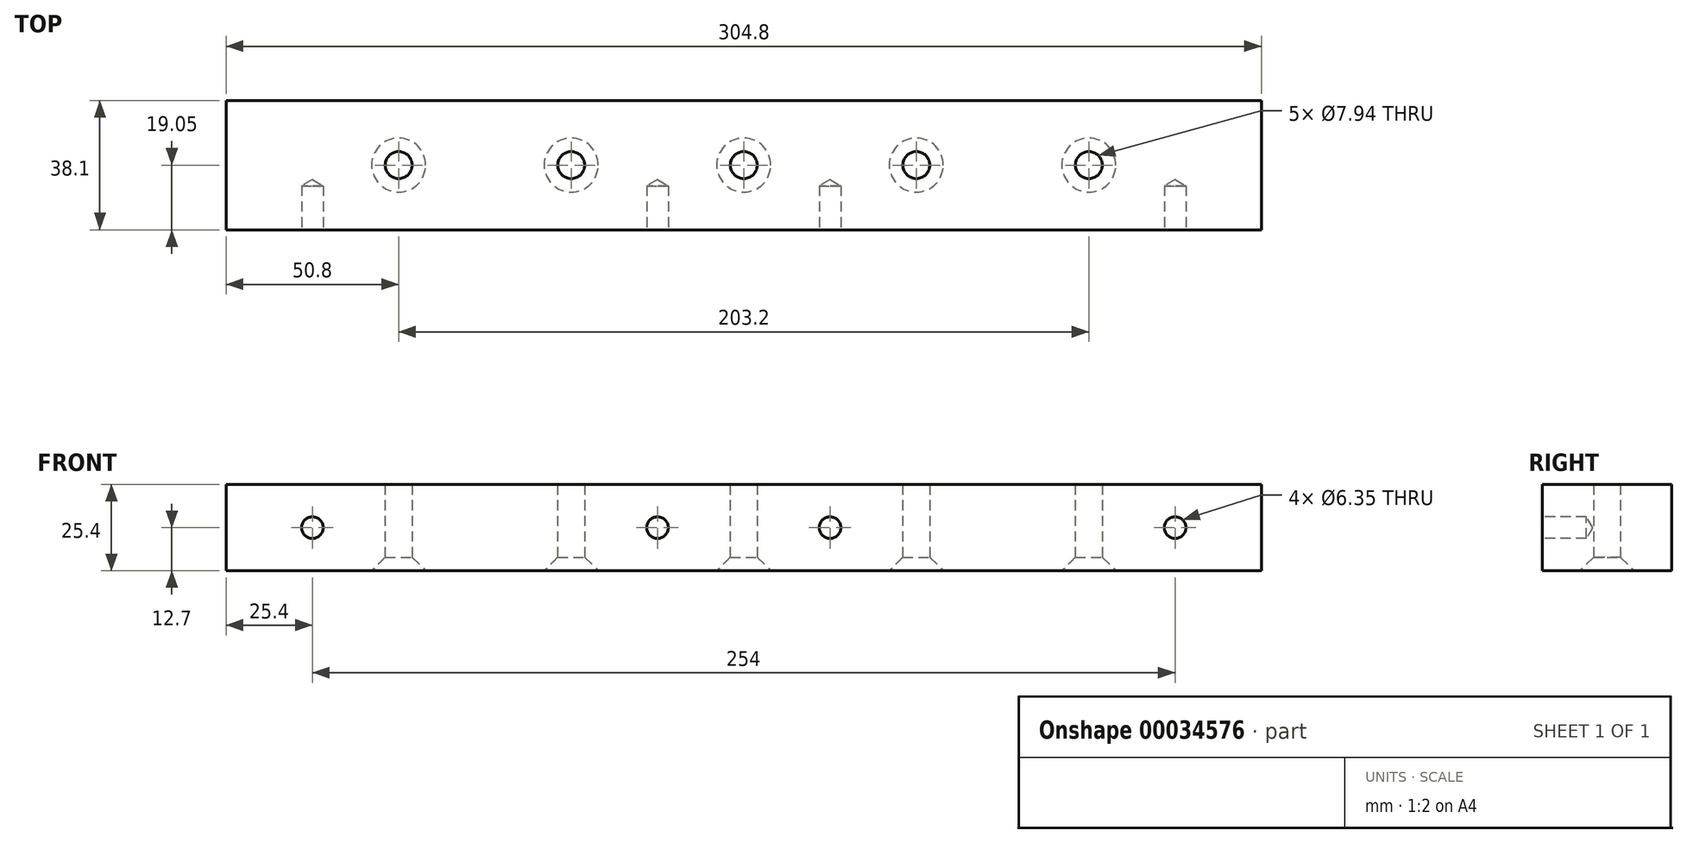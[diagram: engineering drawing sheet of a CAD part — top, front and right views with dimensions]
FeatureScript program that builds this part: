
annotation { "Feature Type Name" : "Feature", "Feature Type Description" : "" }
export const myFeature = defineFeature(function(context is Context, id is Id, definition is map)
    precondition{}
    {
        {
            var Q0;
            Q0=qCreatedBy(makeId("Top.planeOp"),FACE);
            var sketch = newSketch(context, id + "F0", { "sketchPlane" : qUnion([Q0])});
            skLineSegment(sketch, "E0.bottom", {"start": v(0, 0) * mm, "end": v(304.8, 0) * mm});
            skLineSegment(sketch, "E0.top", {"start": v(0, 38.1) * mm, "end": v(304.8, 38.1) * mm});
            skLineSegment(sketch, "E0.left", {"start": v(0, 0) * mm, "end": v(0, 38.1) * mm});
            skLineSegment(sketch, "E0.right", {"start": v(304.8, 0) * mm, "end": v(304.8, 38.1) * mm});
            skPoint(sketch, "E1", {"position": v(50.8, 19.05) * mm});
            skPoint(sketch, "E2", {"position": v(101.6, 19.05) * mm});
            skPoint(sketch, "E3", {"position": v(152.4, 19.05) * mm});
            skPoint(sketch, "E4", {"position": v(203.2, 19.05) * mm});
            skPoint(sketch, "E5", {"position": v(254, 19.05) * mm});
            skSolve(sketch);
        }
        {
            var Q0;
            Q0 = qSketchRegion(id + "F0", true);
            extrude(context, id + "F1", {"entities" : qUnion([Q0]), "depth" : 25.4 * mm});
        }
        {
            var Q0;
            Q0=sQuery(id+"F0.wireOp",VERTEX,"E1");
            var Q1;
            Q1=sQuery(id+"F0.wireOp",VERTEX,"E2");
            var Q2;
            Q2=sQuery(id+"F0.wireOp",VERTEX,"E3");
            var Q3;
            Q3=sQuery(id+"F0.wireOp",VERTEX,"E4");
            var Q4;
            Q4=sQuery(id+"F0.wireOp",VERTEX,"E5");
            var Q5;
            Q5=makeQuery(id+"F1.opExtrude","SWEPT_BODY",BODY,{"disambiguationData":[OSD([sQuery(id+"F0.wireOp",EDGE,"E0.bottom"),sQuery(id+"F0.wireOp",EDGE,"E0.top"),sQuery(id+"F0.wireOp",EDGE,"E0.left"),sQuery(id+"F0.wireOp",EDGE,"E0.right")])]});
            hole(context, id + "F2", {"style" : HoleStyle.C_SINK, "holeDiameter" : 7.94 * mm, "cSinkDiameter" : 15.9 * mm, "endStyle" : HoleEndStyle.THROUGH, "oppositeDirection" : true, "locations" : qUnion([Q0, Q1, Q2, Q3, Q4]), "scope" : qUnion([Q5]), "cSinkAngle" : 90 * degree});
        }
        {
            var Q0;
            Q0=makeQuery(id+"F1.opExtrude","SWEPT_FACE",FACE,{"disambiguationData":[OSD([sQuery(id+"F0.wireOp",EDGE,"E0.bottom")])]});
            var sketch = newSketch(context, id + "F3", { "sketchPlane" : qUnion([Q0])});
            skPoint(sketch, "E6", {"position": v(25.4, 12.7) * mm});
            skPoint(sketch, "E7", {"position": v(127, 12.7) * mm});
            skPoint(sketch, "E8", {"position": v(177.8, 12.7) * mm});
            skPoint(sketch, "E9", {"position": v(279.4, 12.7) * mm});
            skSolve(sketch);
        }
        {
            var Q0;
            Q0=sQuery(id+"F3.wireOp",VERTEX,"E6");
            var Q1;
            Q1=sQuery(id+"F3.wireOp",VERTEX,"E7");
            var Q2;
            Q2=sQuery(id+"F3.wireOp",VERTEX,"E8");
            var Q3;
            Q3=sQuery(id+"F3.wireOp",VERTEX,"E9");
            var Q4;
            Q4=makeQuery(id+"F1.opExtrude","SWEPT_BODY",BODY,{"disambiguationData":[OSD([sQuery(id+"F0.wireOp",EDGE,"E0.bottom"),sQuery(id+"F0.wireOp",EDGE,"E0.top"),sQuery(id+"F0.wireOp",EDGE,"E0.left"),sQuery(id+"F0.wireOp",EDGE,"E0.right")])]});
            hole(context, id + "F4", {"style" : HoleStyle.SIMPLE, "holeDiameter" : 6.35 * mm, "endStyle" : HoleEndStyle.BLIND, "holeDepth" : 12.95 * mm, "locations" : qUnion([Q0, Q1, Q2, Q3]), "scope" : qUnion([Q4])});
        }
    });
